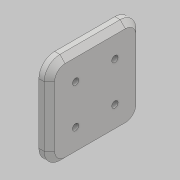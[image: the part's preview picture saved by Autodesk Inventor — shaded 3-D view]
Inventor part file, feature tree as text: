
AUTODESK INVENTOR PART (.ipt)
format: ipt  version: 2018 (Build 220112000, 112)  size: 135,680 bytes
history: native  units: mm
features: sketch x3, hole x2, other x1, extrude x1, fillet x1, chamfer x1, projected_geometry x1
ambient origin geometry x8: Origin, YZ Plane, XZ Plane, XY Plane, X Axis, Y Axis, Z Axis, Center Point
bodies: Body1 (feature_tree)
feature tree (10):
  other  "實體1"
  extrude  "擠出1"  Depth=175.0mm
  fillet  "圓角1"  Radius=175.0mm
  chamfer  "倒角1"  Distance=20.0mm
  hole  "孔1"  [1 undecoded]
  hole  "孔2"  [1 undecoded]
  sketch  "草圖1"
  sketch  "草圖2"
  sketch  "草圖3"
  projected_geometry  "投影迴路1"
note: 2 required parameter values undecoded (feature->parameter linkage not recoverable at this tier; creation-order binding heuristic only, values carry confidence <= 0.55)
